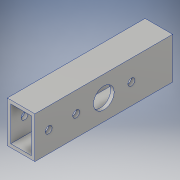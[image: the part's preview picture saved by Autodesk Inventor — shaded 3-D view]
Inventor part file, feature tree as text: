
AUTODESK INVENTOR PART (.ipt)
format: ipt  version: 2017 (Build 210142000, 142)  size: 128,512 bytes
history: native  units: in
note: dims shown in document units (in); Inventor stores cm internally (conversion verified against a paired STEP export)
features: extrude x2, hole x2, sketch x2, pattern_linear x1
ambient origin geometry x8: Origin, YZ Plane, XZ Plane, XY Plane, X Axis, Y Axis, Z Axis, Center Point
bodies: Solid1 (feature_tree)
feature tree (7):
  extrude  "Extrusion1"  Depth=1.5in
  extrude  "Extrusion2"  Depth=5.0in TaperAngle=0.0deg
  pattern_linear  "Rectangular Pattern1"  Spacing1=0.25in  [1 undecoded]
  hole  "Hole1"  [1 undecoded]
  hole  "Hole2"  [1 undecoded]
  sketch  "Sketch1"  dims[d0=1.0in d1=1.5in]
  sketch  "Sketch2"  dims[d2=0.125in d3=5.0in d4=0.0in d5=0.25in d6=5.0in d7=0.0in d8=1.5748in d10=1.0in d11=1.0in d12=1.0in d13=0.625in d14=0.75in d15=0.375in d16=0.25in d17=0.5635in d18=1.0in d19=0.8108in d20=1.0in d21=1.0in d22=0.75in d23=0.75in d24=0.375in d25=0.25in d26=0.5635in d27=1.0in d28=0.8108in]
note: 3 required parameter values undecoded (feature->parameter linkage not recoverable at this tier; creation-order binding heuristic only, values carry confidence <= 0.55)
